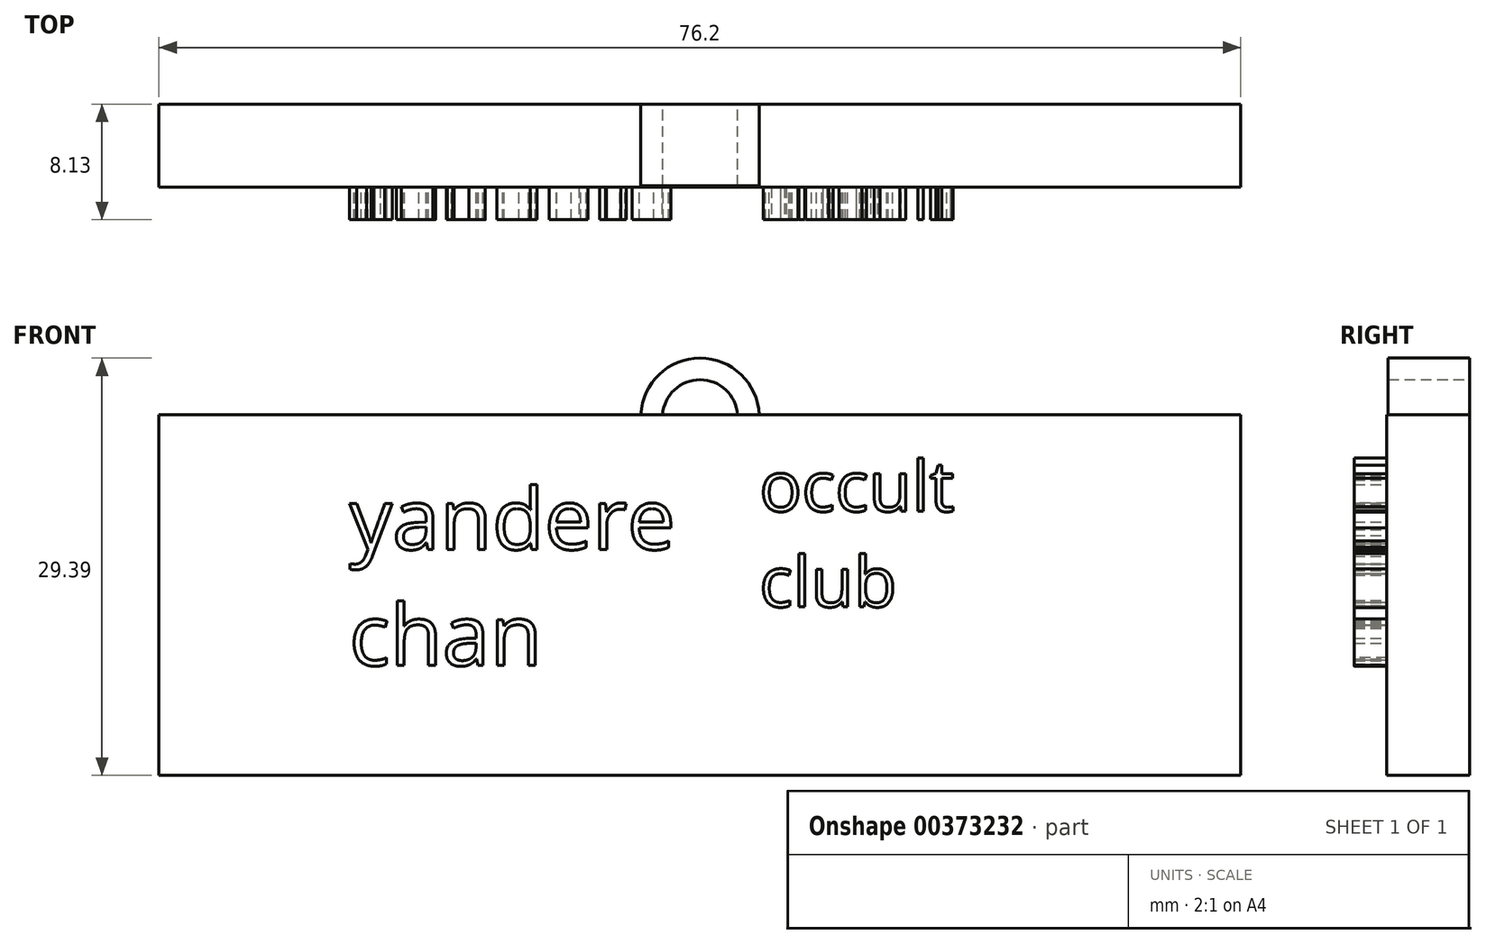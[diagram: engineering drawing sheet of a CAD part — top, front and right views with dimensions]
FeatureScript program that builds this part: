
annotation { "Feature Type Name" : "Feature", "Feature Type Description" : "" }
export const myFeature = defineFeature(function(context is Context, id is Id, definition is map)
    precondition{}
    {
        {
            var Q0;
            Q0=qCreatedBy(makeId("Front.planeOp"),FACE);
            var sketch = newSketch(context, id + "F0", { "sketchPlane" : qUnion([Q0])});
            skLineSegment(sketch, "E0.bottom", {"start": v(-32.61, 21.59) * mm, "end": v(43.59, 21.59) * mm});
            skLineSegment(sketch, "E0.top", {"start": v(-32.61, -3.81) * mm, "end": v(43.59, -3.81) * mm});
            skLineSegment(sketch, "E0.left", {"start": v(-32.61, 21.59) * mm, "end": v(-32.61, -3.81) * mm});
            skLineSegment(sketch, "E0.right", {"start": v(43.59, 21.59) * mm, "end": v(43.59, -3.81) * mm});
            skSolve(sketch);
        }
        {
            var Q0;
            Q0=makeQuery(id+"F0.imprint","IMPRINT",FACE,{"disambiguationData":[TD([[makeQuery(id+"F0.imprint","IMPRINT",EDGE,{"derivedFrom":sQuery(id+"F0.wireOp",EDGE,"E0.bottom")}),-1.0]])]});
            extrude(context, id + "F1", {"entities" : qUnion([Q0]), "depth" : 5.84 * mm});
        }
        {
            var Q0;
            Q0=makeQuery(id+"F1.opExtrude","CAP_FACE",FACE,{"disambiguationData":[OSD([sQuery(id+"F0.wireOp",EDGE,"E0.bottom"),sQuery(id+"F0.wireOp",EDGE,"E0.top"),sQuery(id+"F0.wireOp",EDGE,"E0.left"),sQuery(id+"F0.wireOp",EDGE,"E0.right")])],"isStart":false});
            var sketch = newSketch(context, id + "F2", { "sketchPlane" : qUnion([Q0])});
            skText(sketch, "E1", { "text": "yandere\nchan", "fontName": "OpenSans-Regular.ttf"});
            const initialGuessF2  = {"E1": [-0.0192, 0.0121, 1, 0, 0.00433]};
            skSetInitialGuess(sketch, initialGuessF2);
            skSolve(sketch);
        }
        {
            var Q0;
            Q0 = qSketchRegion(id + "F2", true);
            extrude(context, id + "F3", {"entities" : qUnion([Q0]), "operationType" : NewBodyOperationType.ADD, "depth" : 2.3 * mm});
        }
        {
            var Q0;
            Q0=qCreatedBy(makeId("Front.planeOp"),FACE);
            var sketch = newSketch(context, id + "F4", { "sketchPlane" : qUnion([Q0])});
            skText(sketch, "E2", { "text": "occult \nclub", "fontName": "OpenSans-Regular.ttf"});
            const initialGuessF4  = {"E2": [0.00969, 0.01478, 1, 0, 0.00356]};
            skSetInitialGuess(sketch, initialGuessF4);
            skSolve(sketch);
        }
        {
            var Q0;
            Q0 = qSketchRegion(id + "F4", true);
            extrude(context, id + "F5", {"entities" : qUnion([Q0]), "operationType" : NewBodyOperationType.ADD, "depth" : 8.13 * mm});
        }
        {
            var Q0;
            Q0=qCreatedBy(makeId("Front.planeOp"),FACE);
            var sketch = newSketch(context, id + "F6", { "sketchPlane" : qUnion([Q0])});
            skArc(sketch, "E3", {"start": v(9.67, 21.57) * mm, "mid": v(5.5, 25.58) * mm, "end": v(1.34, 21.56) * mm});
            skArc(sketch, "E4.0", {"start": v(8.15, 21.55) * mm, "mid": v(5.52, 24.06) * mm, "end": v(2.86, 21.58) * mm});
            skLineSegment(sketch, "E5", {"start": v(1.34, 21.56) * mm, "end": v(2.86, 21.58) * mm});
            skLineSegment(sketch, "E6", {"start": v(8.15, 21.55) * mm, "end": v(9.67, 21.57) * mm});
            skSolve(sketch);
        }
        {
            var Q0;
            Q0=makeQuery(id+"F6.imprint","IMPRINT",FACE,{"disambiguationData":[TD([[makeQuery(id+"F6.imprint","IMPRINT",EDGE,{"derivedFrom":sQuery(id+"F6.wireOp",EDGE,"E3")}),1.0]])]});
            extrude(context, id + "F7", {"entities" : qUnion([Q0]), "operationType" : NewBodyOperationType.ADD, "depth" : 5.74 * mm});
        }
    });
